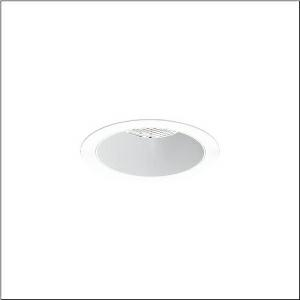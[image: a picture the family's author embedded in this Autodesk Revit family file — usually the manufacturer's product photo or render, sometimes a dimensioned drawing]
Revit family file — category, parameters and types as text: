
# Revit family: lunis_21_l_51db18td91c
name_source: partatom
category: Lighting Fixtures
units: mm (PartAtom-declared; Revit-internal decimal feet)

## family parameters
Cut with Voids When Loaded = No
Host = Face
Light Source = No
Part Type = Normal
Room Calculation Point = No
Round Connector Dimension = Use Diameter
Shared = No

## types (1)
- --- (1 x LED 3000 K ... 6500 K, 4060 lm, 25.4 W, 4000K)
    Apparent Load = 25 VA
    CIE Flux Codes = 87 97 99 100 100
    Color Rendering = 80
    Color Temperature = 4000K
    Default Elevation = 1800 mm
    Description = Lunis 21,  L, downlight, light control with lens, of PMMA, anti glare with reflector, of aluminium, light emission: direct distribution, LED rated luminous flux: 4.060lm, light colour: 8tw, with terminal, 5-pole, mains connection: 220..240V, AC/DC, 0/50..60Hz, housing, round, of diecast aluminium, traffic white (RAL 9016), diameter: 165mm, clamping range: 1..40mm, protection rating (complete): IP20, protection rating (on room side): IP54, insulation class (complete): insulation class II (safety insulation), certification: CE, impact resistance: IK03, packaging unit: 1 piece
    Height = 0 mm  [stored 0 ft]
    Lamp = 1 x LED 3000 K ... 6500 K
    Lamp Light Flux = 4060 lm
    Lamp Power = 25.4 W
    Lamp count = 1
    Length = 165 mm
    Luminous efficacy = 160 lm/W
    Manufacturer = Siteco
    ModVariant = No
    Model = 51DB18TD91C
    Mounting Place = Ceiling
    Mounting Type = Recessed
    Number of Poles = 1
    OnlyDefault = Yes
    Power Factor = 1
    Product Name = Lunis 21 L
    Product group = downlight
    ProductGroupID = 400
    Protection Class = Protection class II
    Protection Degree = IP 20
    RLX_Detail_Level = 1
    RLX_Emergency_Light_Flux = 0 lm
    RLX_Emergency_Type = 0
    RLX_Emergency_Type_DB = No
    RlxData = <blob elided: 13541 chars, md5=7a7ec6aa>
    Socket = socket
    Standby Power = 0 W
    System Light Flux = 4060 lm
    System Power = 25 W
    Type Comments = individual setting: CCT=4000K, colour temperature 4000K, luminous flux: 100 % | (ON | ON | OFF | OFF) | 700 mA
    Type Image = l_1291155.jpg
    URL = http://relux.com
    VarID = @adj_019360
    Voltage = 0 V
    Weight = 0.00 kg
    Width = 0 mm  [stored 0 ft]

note: [stored X ft] marks values corroborated as IEEE doubles in the binary element streams (Revit-internal decimal feet)

## geometry (parser evidence)
native form markers: Sweep x9
no freeform markers — native parametric forms only
